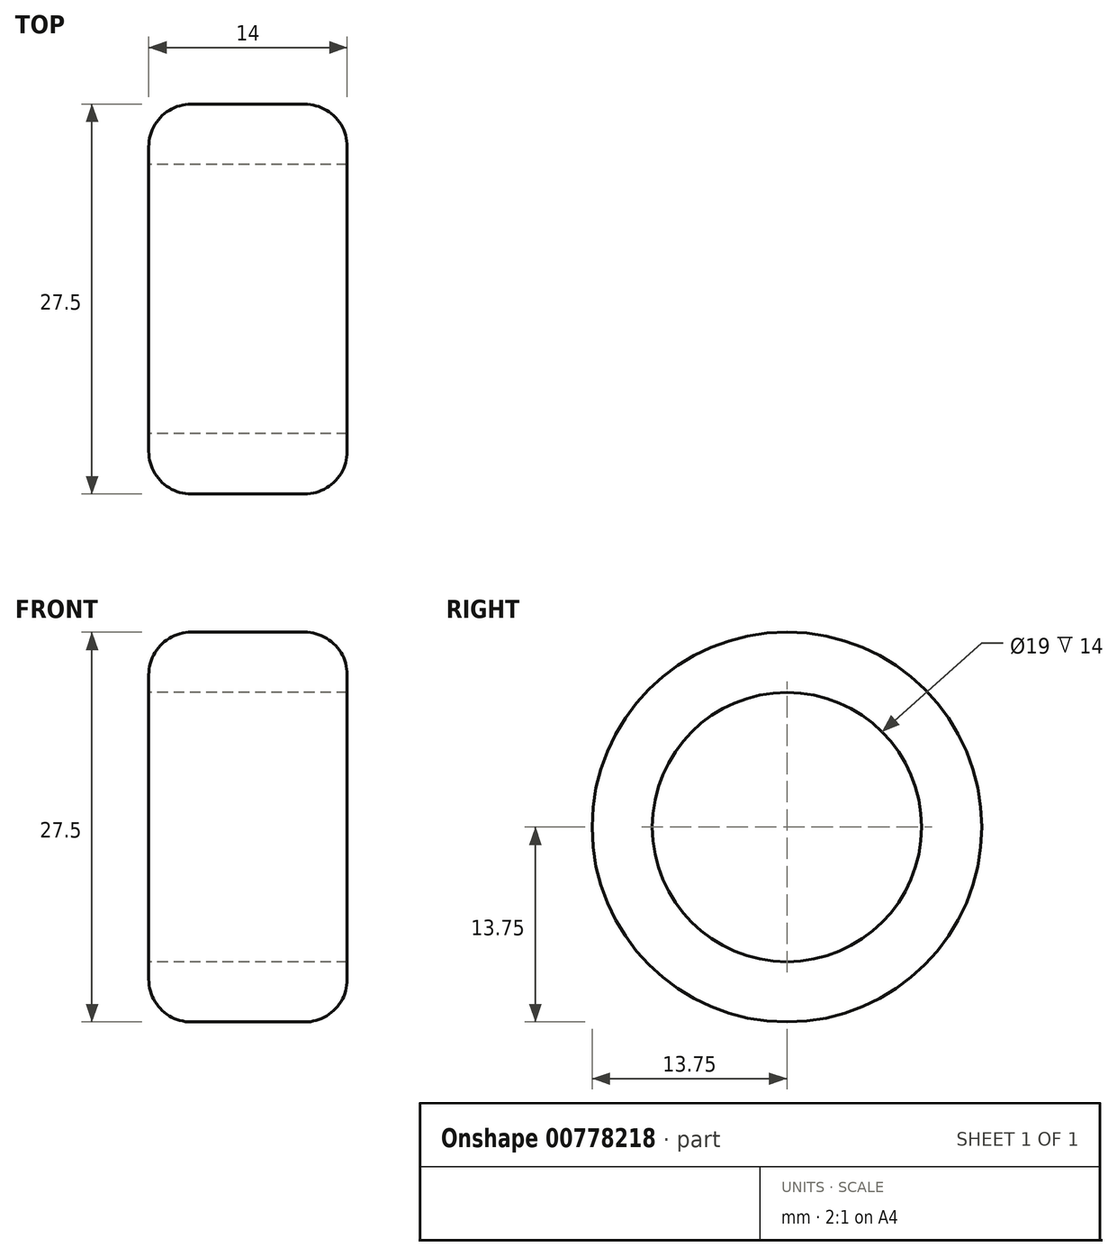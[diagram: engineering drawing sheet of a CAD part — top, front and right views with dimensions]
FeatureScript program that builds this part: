
annotation { "Feature Type Name" : "Feature", "Feature Type Description" : "" }
export const myFeature = defineFeature(function(context is Context, id is Id, definition is map)
    precondition{}
    {
        {
            var Q0;
            Q0=qCreatedBy(makeId("Right.planeOp"),FACE);
            var sketch = newSketch(context, id + "F0", { "sketchPlane" : qUnion([Q0])});
            skCircle(sketch, "E0", {"center": v(0, 0) * mm, "radius": 9.5 * mm});
            skCircle(sketch, "E1", {"center": v(0, 0) * mm, "radius": 13.75 * mm});
            skSolve(sketch);
        }
        {
            var Q0;
            Q0=makeQuery(id+"F0.imprint","IMPRINT",FACE,{"disambiguationData":[TD([[makeQuery(id+"F0.imprint","IMPRINT",EDGE,{"derivedFrom":sQuery(id+"F0.wireOp",EDGE,"E0")}),-1.0]])]});
            extrude(context, id + "F1", {"entities" : qUnion([Q0]), "depth" : 14 * mm, "offsetDistance" : 25 * mm});
        }
        {
            var Q0;
            Q0=makeQuery(id+"F1.opExtrude","CAP_EDGE",EDGE,{"disambiguationData":[OSD([sQuery(id+"F0.wireOp",EDGE,"E1")])],"isStart":false});
            var Q1;
            Q1=makeQuery(id+"F1.opExtrude","CAP_EDGE",EDGE,{"disambiguationData":[OSD([sQuery(id+"F0.wireOp",EDGE,"E1")])],"isStart":true});
            fillet(context, id + "F2", {"entities" : qUnion([Q0, Q1]), "radius" : 3 * mm, "tangentPropagation" : true, "allowEdgeOverflow" : false});
        }
    });
